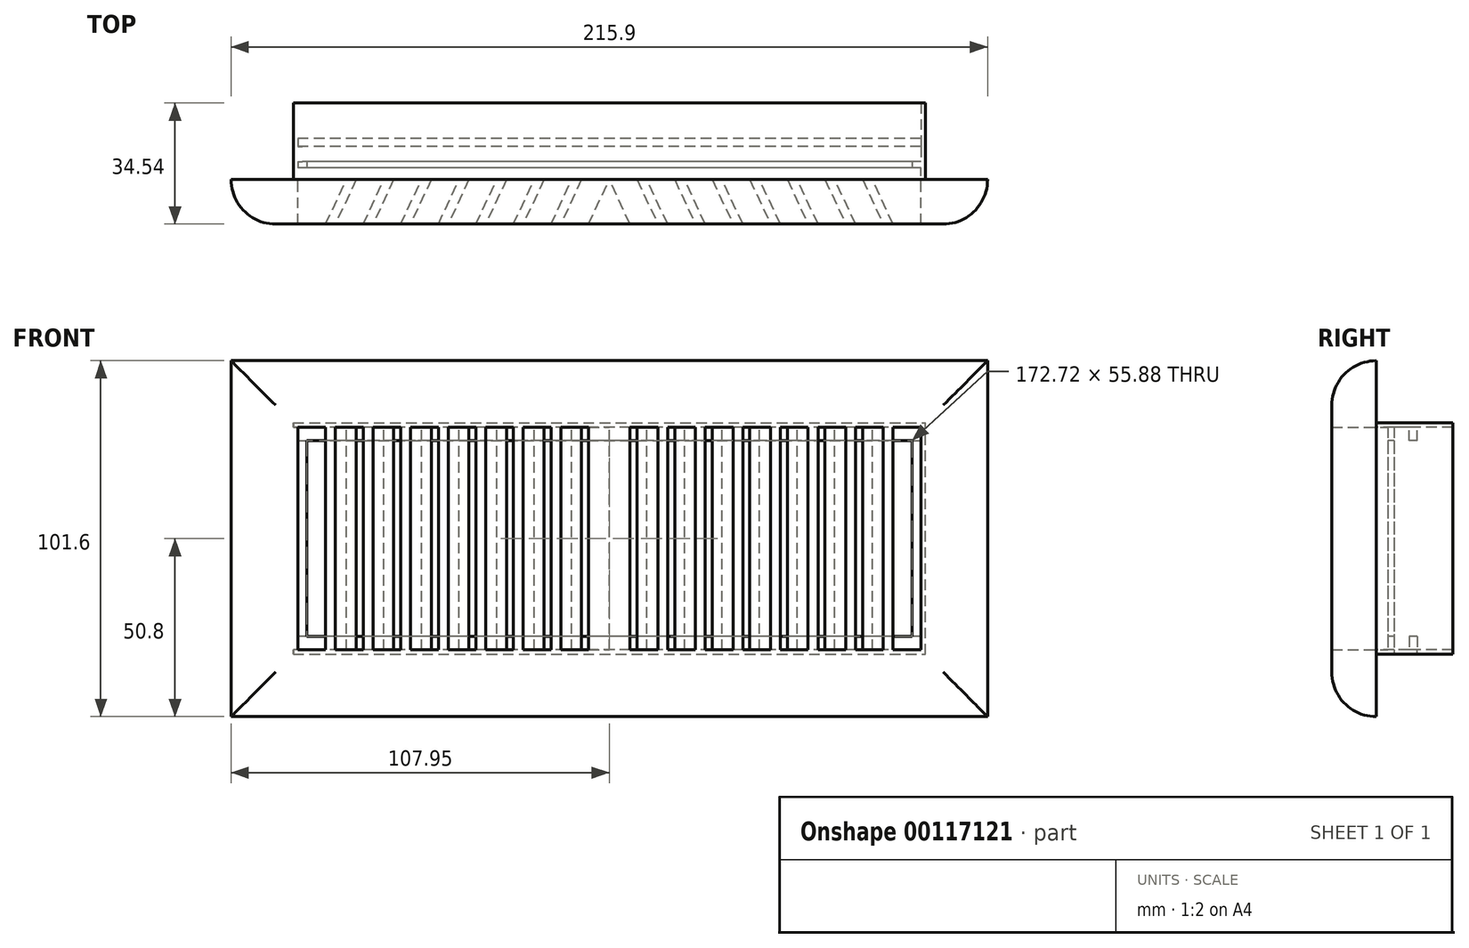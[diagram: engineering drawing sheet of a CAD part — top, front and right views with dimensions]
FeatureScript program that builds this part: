
annotation { "Feature Type Name" : "Feature", "Feature Type Description" : "" }
export const myFeature = defineFeature(function(context is Context, id is Id, definition is map)
    precondition{}
    {
        {
            var Q0;
            Q0=qCreatedBy(makeId("Front.planeOp"),FACE);
            var sketch = newSketch(context, id + "F0", { "sketchPlane" : qUnion([Q0])});
            skLineSegment(sketch, "E0.bottom", {"start": v(107.95, -50.8) * mm, "end": v(-107.95, -50.8) * mm});
            skLineSegment(sketch, "E0.top", {"start": v(107.95, 50.8) * mm, "end": v(-107.95, 50.8) * mm});
            skLineSegment(sketch, "E0.left", {"start": v(107.95, -50.8) * mm, "end": v(107.95, 50.8) * mm});
            skLineSegment(sketch, "E0.right", {"start": v(-107.95, -50.8) * mm, "end": v(-107.95, 50.8) * mm});
            skPoint(sketch, "E0.middle", {"position": v(0, 0) * mm});
            skLineSegment(sketch, "E1.bottom", {"start": v(88.9, -31.75) * mm, "end": v(-88.9, -31.75) * mm});
            skLineSegment(sketch, "E1.top", {"start": v(88.9, 31.75) * mm, "end": v(-88.9, 31.75) * mm});
            skLineSegment(sketch, "E1.left", {"start": v(88.9, -31.75) * mm, "end": v(88.9, 31.75) * mm});
            skLineSegment(sketch, "E1.right", {"start": v(-88.9, -31.75) * mm, "end": v(-88.9, 31.75) * mm});
            skSolve(sketch);
        }
        {
            var Q0;
            Q0=makeQuery(id+"F0.imprint","IMPRINT",FACE,{"disambiguationData":[TD([[makeQuery(id+"F0.imprint","IMPRINT",EDGE,{"derivedFrom":sQuery(id+"F0.wireOp",EDGE,"E0.bottom")}),-1.0]])]});
            extrude(context, id + "F1", {"entities" : qUnion([Q0]), "depth" : 12.7 * mm});
        }
        {
            var Q0;
            Q0=makeQuery(id+"F1.opExtrude","SWEPT_FACE",FACE,{"disambiguationData":[OSD([sQuery(id+"F0.wireOp",EDGE,"E0.top")])]});
            var sketch = newSketch(context, id + "F2", { "sketchPlane" : qUnion([Q0])});
            skLineSegment(sketch, "E2", {"start": v(-75.05, 0) * mm, "end": v(-80.97, -12.7) * mm});
            skLineSegment(sketch, "E3", {"start": v(-80.97, -12.7) * mm, "end": v(-78.17, -12.7) * mm});
            skLineSegment(sketch, "E4", {"start": v(-78.17, -12.7) * mm, "end": v(-72.25, 0) * mm});
            skLineSegment(sketch, "E5", {"start": v(-72.25, 0) * mm, "end": v(-75.05, 0) * mm});
            skLineSegment(sketch, "E6.1.0.0", {"start": v(-64.33, 0) * mm, "end": v(-70.25, -12.7) * mm});
            skLineSegment(sketch, "E6.1.0.1", {"start": v(-70.25, -12.7) * mm, "end": v(-67.45, -12.7) * mm});
            skLineSegment(sketch, "E6.1.0.2", {"start": v(-67.45, -12.7) * mm, "end": v(-61.53, 0) * mm});
            skLineSegment(sketch, "E6.1.0.3", {"start": v(-61.53, 0) * mm, "end": v(-64.33, 0) * mm});
            skLineSegment(sketch, "E6.2.0.0", {"start": v(-53.6, 0) * mm, "end": v(-59.53, -12.7) * mm});
            skLineSegment(sketch, "E6.2.0.1", {"start": v(-59.53, -12.7) * mm, "end": v(-56.73, -12.7) * mm});
            skLineSegment(sketch, "E6.2.0.2", {"start": v(-56.73, -12.7) * mm, "end": v(-50.8, 0) * mm});
            skLineSegment(sketch, "E6.2.0.3", {"start": v(-50.8, 0) * mm, "end": v(-53.6, 0) * mm});
            skLineSegment(sketch, "E6.3.0.0", {"start": v(-42.88, 0) * mm, "end": v(-48.8, -12.7) * mm});
            skLineSegment(sketch, "E6.3.0.1", {"start": v(-48.8, -12.7) * mm, "end": v(-46, -12.7) * mm});
            skLineSegment(sketch, "E6.3.0.2", {"start": v(-46, -12.7) * mm, "end": v(-40.08, 0) * mm});
            skLineSegment(sketch, "E6.3.0.3", {"start": v(-40.08, 0) * mm, "end": v(-42.88, 0) * mm});
            skLineSegment(sketch, "E6.4.0.0", {"start": v(-32.16, 0) * mm, "end": v(-38.08, -12.7) * mm});
            skLineSegment(sketch, "E6.4.0.1", {"start": v(-38.08, -12.7) * mm, "end": v(-35.28, -12.7) * mm});
            skLineSegment(sketch, "E6.4.0.2", {"start": v(-35.28, -12.7) * mm, "end": v(-29.36, 0) * mm});
            skLineSegment(sketch, "E6.4.0.3", {"start": v(-29.36, 0) * mm, "end": v(-32.16, 0) * mm});
            skLineSegment(sketch, "E6.5.0.0", {"start": v(-21.44, 0) * mm, "end": v(-27.36, -12.7) * mm});
            skLineSegment(sketch, "E6.5.0.1", {"start": v(-27.36, -12.7) * mm, "end": v(-24.56, -12.7) * mm});
            skLineSegment(sketch, "E6.5.0.2", {"start": v(-24.56, -12.7) * mm, "end": v(-18.64, 0) * mm});
            skLineSegment(sketch, "E6.5.0.3", {"start": v(-18.64, 0) * mm, "end": v(-21.44, 0) * mm});
            skLineSegment(sketch, "E6.6.0.0", {"start": v(-10.72, 0) * mm, "end": v(-16.64, -12.7) * mm});
            skLineSegment(sketch, "E6.6.0.1", {"start": v(-16.64, -12.7) * mm, "end": v(-13.84, -12.7) * mm});
            skLineSegment(sketch, "E6.6.0.2", {"start": v(-13.84, -12.7) * mm, "end": v(-7.92, 0) * mm});
            skLineSegment(sketch, "E6.6.0.3", {"start": v(-7.92, 0) * mm, "end": v(-10.72, 0) * mm});
            skLineSegment(sketch, "E6.direction1", {"start": v(-80.97, -12.7) * mm, "end": v(-70.25, -12.7) * mm, "construction": true});
            skLineSegment(sketch, "E7", {"start": v(75.05, 0) * mm, "end": v(80.97, -12.7) * mm});
            skLineSegment(sketch, "E8", {"start": v(80.97, -12.7) * mm, "end": v(78.17, -12.7) * mm});
            skLineSegment(sketch, "E9", {"start": v(78.17, -12.7) * mm, "end": v(72.25, 0) * mm});
            skLineSegment(sketch, "E10", {"start": v(72.25, 0) * mm, "end": v(75.05, 0) * mm});
            skLineSegment(sketch, "E11.1.0.0", {"start": v(70.25, -12.7) * mm, "end": v(67.45, -12.7) * mm});
            skLineSegment(sketch, "E11.1.0.1", {"start": v(64.33, 0) * mm, "end": v(70.25, -12.7) * mm});
            skLineSegment(sketch, "E11.1.0.2", {"start": v(61.53, 0) * mm, "end": v(64.33, 0) * mm});
            skLineSegment(sketch, "E11.1.0.3", {"start": v(67.45, -12.7) * mm, "end": v(61.53, 0) * mm});
            skLineSegment(sketch, "E11.2.0.0", {"start": v(59.53, -12.7) * mm, "end": v(56.73, -12.7) * mm});
            skLineSegment(sketch, "E11.2.0.1", {"start": v(53.6, 0) * mm, "end": v(59.53, -12.7) * mm});
            skLineSegment(sketch, "E11.2.0.2", {"start": v(50.8, 0) * mm, "end": v(53.6, 0) * mm});
            skLineSegment(sketch, "E11.2.0.3", {"start": v(56.73, -12.7) * mm, "end": v(50.8, 0) * mm});
            skLineSegment(sketch, "E11.3.0.0", {"start": v(48.8, -12.7) * mm, "end": v(46, -12.7) * mm});
            skLineSegment(sketch, "E11.3.0.1", {"start": v(42.88, 0) * mm, "end": v(48.8, -12.7) * mm});
            skLineSegment(sketch, "E11.3.0.2", {"start": v(40.08, 0) * mm, "end": v(42.88, 0) * mm});
            skLineSegment(sketch, "E11.3.0.3", {"start": v(46, -12.7) * mm, "end": v(40.08, 0) * mm});
            skLineSegment(sketch, "E11.4.0.0", {"start": v(38.08, -12.7) * mm, "end": v(35.28, -12.7) * mm});
            skLineSegment(sketch, "E11.4.0.1", {"start": v(32.16, 0) * mm, "end": v(38.08, -12.7) * mm});
            skLineSegment(sketch, "E11.4.0.2", {"start": v(29.36, 0) * mm, "end": v(32.16, 0) * mm});
            skLineSegment(sketch, "E11.4.0.3", {"start": v(35.28, -12.7) * mm, "end": v(29.36, 0) * mm});
            skLineSegment(sketch, "E11.5.0.0", {"start": v(27.36, -12.7) * mm, "end": v(24.56, -12.7) * mm});
            skLineSegment(sketch, "E11.5.0.1", {"start": v(21.44, 0) * mm, "end": v(27.36, -12.7) * mm});
            skLineSegment(sketch, "E11.5.0.2", {"start": v(18.64, 0) * mm, "end": v(21.44, 0) * mm});
            skLineSegment(sketch, "E11.5.0.3", {"start": v(24.56, -12.7) * mm, "end": v(18.64, 0) * mm});
            skLineSegment(sketch, "E11.6.0.0", {"start": v(16.64, -12.7) * mm, "end": v(13.84, -12.7) * mm});
            skLineSegment(sketch, "E11.6.0.1", {"start": v(10.72, 0) * mm, "end": v(16.64, -12.7) * mm});
            skLineSegment(sketch, "E11.6.0.2", {"start": v(7.92, 0) * mm, "end": v(10.72, 0) * mm});
            skLineSegment(sketch, "E11.6.0.3", {"start": v(13.84, -12.7) * mm, "end": v(7.92, 0) * mm});
            skLineSegment(sketch, "E11.direction1", {"start": v(78.17, -12.7) * mm, "end": v(67.45, -12.7) * mm, "construction": true});
            skLineSegment(sketch, "E12", {"start": v(0, 0) * mm, "end": v(0, -12.7) * mm, "construction": true});
            skLineSegment(sketch, "E13", {"start": v(0, 0) * mm, "end": v(-5.92, -12.7) * mm});
            skLineSegment(sketch, "E14", {"start": v(0, 0) * mm, "end": v(5.92, -12.7) * mm});
            skLineSegment(sketch, "E15", {"start": v(-5.92, -12.7) * mm, "end": v(5.92, -12.7) * mm});
            skSolve(sketch);
        }
        {
            var Q0;
            Q0 = qSketchRegion(id + "F2", true);
            extrude(context, id + "F3", {"entities" : qUnion([Q0]), "operationType" : NewBodyOperationType.ADD, "oppositeDirection" : true, "depth" : 101.6 * mm});
        }
        {
            var Q0;
            Q0=makeQuery(id+"F1.opExtrude","CAP_EDGE",EDGE,{"disambiguationData":[OSD([sQuery(id+"F0.wireOp",EDGE,"E0.top")])],"isStart":false});
            var Q1;
            Q1=makeQuery(id+"F1.opExtrude","CAP_EDGE",EDGE,{"disambiguationData":[OSD([sQuery(id+"F0.wireOp",EDGE,"E0.right")])],"isStart":false});
            var Q2;
            Q2=makeQuery(id+"F1.opExtrude","CAP_EDGE",EDGE,{"disambiguationData":[OSD([sQuery(id+"F0.wireOp",EDGE,"E0.bottom")])],"isStart":false});
            var Q3;
            Q3=makeQuery(id+"F1.opExtrude","CAP_EDGE",EDGE,{"disambiguationData":[OSD([sQuery(id+"F0.wireOp",EDGE,"E0.left")])],"isStart":false});
            fillet(context, id + "F4", {"entities" : qUnion([Q0, Q1, Q2, Q3]), "radius" : 12.7 * mm, "tangentPropagation" : true, "allowEdgeOverflow" : false});
        }
        {
            var Q0;
            Q0=makeQuery(id+"F3.boolean.opBoolean","MERGE",FACE,{"derivedFrom":[makeQuery(id+"F1.opExtrude","CAP_FACE",FACE,{"disambiguationData":[OSD([sQuery(id+"F0.wireOp",EDGE,"E0.bottom"),sQuery(id+"F0.wireOp",EDGE,"E0.top"),sQuery(id+"F0.wireOp",EDGE,"E0.left"),sQuery(id+"F0.wireOp",EDGE,"E0.right"),sQuery(id+"F0.wireOp",EDGE,"E1.bottom"),sQuery(id+"F0.wireOp",EDGE,"E1.top"),sQuery(id+"F0.wireOp",EDGE,"E1.left"),sQuery(id+"F0.wireOp",EDGE,"E1.right")])],"isStart":true}),makeQuery(id+"F3.opExtrude","SWEPT_FACE",FACE,{"disambiguationData":[OSD([sQuery(id+"F2.wireOp",EDGE,"E5")])]}),makeQuery(id+"F3.opExtrude","SWEPT_FACE",FACE,{"disambiguationData":[OSD([sQuery(id+"F2.wireOp",EDGE,"E6.1.0.3")])]}),makeQuery(id+"F3.opExtrude","SWEPT_FACE",FACE,{"disambiguationData":[OSD([sQuery(id+"F2.wireOp",EDGE,"E6.2.0.3")])]}),makeQuery(id+"F3.opExtrude","SWEPT_FACE",FACE,{"disambiguationData":[OSD([sQuery(id+"F2.wireOp",EDGE,"E6.3.0.3")])]}),makeQuery(id+"F3.opExtrude","SWEPT_FACE",FACE,{"disambiguationData":[OSD([sQuery(id+"F2.wireOp",EDGE,"E6.4.0.3")])]}),makeQuery(id+"F3.opExtrude","SWEPT_FACE",FACE,{"disambiguationData":[OSD([sQuery(id+"F2.wireOp",EDGE,"E6.5.0.3")])]}),makeQuery(id+"F3.opExtrude","SWEPT_FACE",FACE,{"disambiguationData":[OSD([sQuery(id+"F2.wireOp",EDGE,"E6.6.0.3")])]}),makeQuery(id+"F3.opExtrude","SWEPT_FACE",FACE,{"disambiguationData":[OSD([sQuery(id+"F2.wireOp",EDGE,"E10")])]}),makeQuery(id+"F3.opExtrude","SWEPT_FACE",FACE,{"disambiguationData":[OSD([sQuery(id+"F2.wireOp",EDGE,"E11.1.0.2")])]}),makeQuery(id+"F3.opExtrude","SWEPT_FACE",FACE,{"disambiguationData":[OSD([sQuery(id+"F2.wireOp",EDGE,"E11.2.0.2")])]}),makeQuery(id+"F3.opExtrude","SWEPT_FACE",FACE,{"disambiguationData":[OSD([sQuery(id+"F2.wireOp",EDGE,"E11.3.0.2")])]}),makeQuery(id+"F3.opExtrude","SWEPT_FACE",FACE,{"disambiguationData":[OSD([sQuery(id+"F2.wireOp",EDGE,"E11.4.0.2")])]}),makeQuery(id+"F3.opExtrude","SWEPT_FACE",FACE,{"disambiguationData":[OSD([sQuery(id+"F2.wireOp",EDGE,"E11.5.0.2")])]}),makeQuery(id+"F3.opExtrude","SWEPT_FACE",FACE,{"disambiguationData":[OSD([sQuery(id+"F2.wireOp",EDGE,"E11.6.0.2")])]})]});
            var sketch = newSketch(context, id + "F5", { "sketchPlane" : qUnion([Q0])});
            skLineSegment(sketch, "E16.bottom", {"start": v(90.17, -33.02) * mm, "end": v(-90.17, -33.02) * mm});
            skLineSegment(sketch, "E16.top", {"start": v(90.17, 33.02) * mm, "end": v(-90.17, 33.02) * mm});
            skLineSegment(sketch, "E16.right", {"start": v(-90.17, -33.02) * mm, "end": v(-90.17, 33.02) * mm});
            skPoint(sketch, "E16.middle", {"position": v(0, 0) * mm});
            skLineSegment(sketch, "E17.bottom", {"start": v(88.9, -31.75) * mm, "end": v(-88.9, -31.75) * mm});
            skLineSegment(sketch, "E17.top", {"start": v(88.9, 31.75) * mm, "end": v(-88.9, 31.75) * mm});
            skLineSegment(sketch, "E17.right", {"start": v(-88.9, -31.75) * mm, "end": v(-88.9, 31.75) * mm});
            skLineSegment(sketch, "E18", {"start": v(88.9, 31.75) * mm, "end": v(90.17, 31.75) * mm});
            skLineSegment(sketch, "E19", {"start": v(90.17, 31.75) * mm, "end": v(90.17, 33.02) * mm});
            skLineSegment(sketch, "E20", {"start": v(88.9, -31.75) * mm, "end": v(90.17, -31.75) * mm});
            skLineSegment(sketch, "E21", {"start": v(90.17, -31.75) * mm, "end": v(90.17, -33.02) * mm});
            skSolve(sketch);
        }
        {
            var Q0;
            Q0 = qSketchRegion(id + "F5", true);
            extrude(context, id + "F6", {"entities" : qUnion([Q0]), "operationType" : NewBodyOperationType.ADD, "depth" : 3.3 * mm});
        }
        {
            var Q0;
            Q0=makeQuery(id+"F6.opExtrude","CAP_FACE",FACE,{"disambiguationData":[OSD([sQuery(id+"F5.wireOp",EDGE,"E16.bottom"),sQuery(id+"F5.wireOp",EDGE,"E16.top"),sQuery(id+"F5.wireOp",EDGE,"E16.right"),sQuery(id+"F5.wireOp",EDGE,"E17.bottom"),sQuery(id+"F5.wireOp",EDGE,"E17.top"),sQuery(id+"F5.wireOp",EDGE,"E17.right"),sQuery(id+"F5.wireOp",EDGE,"E18"),sQuery(id+"F5.wireOp",EDGE,"E19"),sQuery(id+"F5.wireOp",EDGE,"E20"),sQuery(id+"F5.wireOp",EDGE,"E21")])],"isStart":false});
            var sketch = newSketch(context, id + "F7", { "sketchPlane" : qUnion([Q0])});
            skLineSegment(sketch, "E22.bottom", {"start": v(-90.17, 33.02) * mm, "end": v(88.9, 33.02) * mm});
            skLineSegment(sketch, "E22.top", {"start": v(-90.17, -33.02) * mm, "end": v(88.9, -33.02) * mm});
            skLineSegment(sketch, "E22.left", {"start": v(-90.17, 33.02) * mm, "end": v(-90.17, -33.02) * mm});
            skLineSegment(sketch, "E22.right", {"start": v(88.9, 33.02) * mm, "end": v(88.9, -33.02) * mm});
            skLineSegment(sketch, "E23.bottom", {"start": v(-86.36, 27.94) * mm, "end": v(86.36, 27.94) * mm});
            skLineSegment(sketch, "E23.top", {"start": v(-86.36, -27.94) * mm, "end": v(86.36, -27.94) * mm});
            skLineSegment(sketch, "E23.left", {"start": v(-86.36, 27.94) * mm, "end": v(-86.36, -27.94) * mm});
            skLineSegment(sketch, "E23.right", {"start": v(86.36, 27.94) * mm, "end": v(86.36, -27.94) * mm});
            skSolve(sketch);
        }
        {
            var Q0;
            Q0 = qSketchRegion(id + "F7", true);
            extrude(context, id + "F8", {"entities" : qUnion([Q0]), "operationType" : NewBodyOperationType.ADD, "depth" : 1.78 * mm});
        }
        {
            var Q0;
            Q0=makeQuery(id+"F8.opExtrude","CAP_FACE",FACE,{"disambiguationData":[OSD([sQuery(id+"F7.wireOp",EDGE,"E22.bottom"),sQuery(id+"F7.wireOp",EDGE,"E22.top"),sQuery(id+"F7.wireOp",EDGE,"E22.left"),sQuery(id+"F7.wireOp",EDGE,"E22.right"),sQuery(id+"F7.wireOp",EDGE,"E23.bottom"),sQuery(id+"F7.wireOp",EDGE,"E23.top"),sQuery(id+"F7.wireOp",EDGE,"E23.left"),sQuery(id+"F7.wireOp",EDGE,"E23.right")])],"isStart":false});
            var sketch = newSketch(context, id + "F9", { "sketchPlane" : qUnion([Q0])});
            skLineSegment(sketch, "E24.bottom", {"start": v(-90.17, 33.02) * mm, "end": v(88.9, 33.02) * mm});
            skLineSegment(sketch, "E24.top", {"start": v(-90.17, -33.02) * mm, "end": v(88.9, -33.02) * mm});
            skLineSegment(sketch, "E24.left", {"start": v(-90.17, 33.02) * mm, "end": v(-90.17, -33.02) * mm});
            skLineSegment(sketch, "E25.bottom", {"start": v(-88.9, 31.75) * mm, "end": v(87.63, 31.75) * mm});
            skLineSegment(sketch, "E25.top", {"start": v(-88.9, -31.75) * mm, "end": v(87.63, -31.75) * mm});
            skLineSegment(sketch, "E25.left", {"start": v(-88.9, 31.75) * mm, "end": v(-88.9, -31.75) * mm});
            skLineSegment(sketch, "E26", {"start": v(88.9, -33.02) * mm, "end": v(90.18, -33.02) * mm});
            skLineSegment(sketch, "E27", {"start": v(90.18, -33.02) * mm, "end": v(90.18, -31.75) * mm});
            skLineSegment(sketch, "E28", {"start": v(90.18, -31.75) * mm, "end": v(87.63, -31.75) * mm});
            skLineSegment(sketch, "E29", {"start": v(88.9, 33.02) * mm, "end": v(90.17, 33.02) * mm});
            skLineSegment(sketch, "E30", {"start": v(90.17, 33.02) * mm, "end": v(90.17, 31.75) * mm});
            skLineSegment(sketch, "E31", {"start": v(90.17, 31.75) * mm, "end": v(87.63, 31.75) * mm});
            skSolve(sketch);
        }
        {
            var Q0;
            {var subQ5=sQuery(id+"F9.wireOp",EDGE,"E24.bottom");Q0=makeQuery(id+"F9.imprint","IMPRINT",FACE,{"disambiguationData":[TD([[makeQuery(id+"F9.imprint","IMPRINT",EDGE,{"derivedFrom":subQ5}),1.0]])]});}
            var Q1;
            {var subQ0=sQuery(id+"F9.wireOp",EDGE,"E29");Q1=makeQuery(id+"F9.imprint","IMPRINT",FACE,{"disambiguationData":[TD([[makeQuery(id+"F9.imprint","IMPRINT",EDGE,{"derivedFrom":subQ0}),-1.0]])]});}
            var Q2;
            {var subQ0=sQuery(id+"F9.wireOp",EDGE,"E26");Q2=makeQuery(id+"F9.imprint","IMPRINT",FACE,{"disambiguationData":[TD([[makeQuery(id+"F9.imprint","IMPRINT",EDGE,{"derivedFrom":subQ0}),1.0]])]});}
            extrude(context, id + "F10", {"entities" : qUnion([Q0, Q1, Q2]), "operationType" : NewBodyOperationType.ADD, "depth" : 4.32 * mm});
        }
        {
            var Q0;
            {var subQ0=sQuery(id+"F5.wireOp",EDGE,"E21");var subQ1=sQuery(id+"F5.wireOp",EDGE,"E20");var subQ2=sQuery(id+"F5.wireOp",EDGE,"E17.bottom");var subQ3=sQuery(id+"F5.wireOp",EDGE,"E16.bottom");Q0=makeQuery(id+"F8.boolean.opBoolean","SPLIT",FACE,{"disambiguationData":[TD([makeQuery(id+"F1.opExtrude","SWEPT_FACE",FACE,{"disambiguationData":[OSD([sQuery(id+"F0.wireOp",EDGE,"E1.bottom")])]})])],"derivedFrom":makeQuery(id+"F6.opExtrude","CAP_FACE",FACE,{"disambiguationData":[OSD([subQ3,sQuery(id+"F5.wireOp",EDGE,"E16.top"),sQuery(id+"F5.wireOp",EDGE,"E16.right"),subQ2,sQuery(id+"F5.wireOp",EDGE,"E17.top"),sQuery(id+"F5.wireOp",EDGE,"E17.right"),sQuery(id+"F5.wireOp",EDGE,"E18"),sQuery(id+"F5.wireOp",EDGE,"E19"),subQ1,subQ0])],"isStart":false})});}
            var sketch = newSketch(context, id + "F11", { "sketchPlane" : qUnion([Q0])});
            skLineSegment(sketch, "E32.bottom", {"start": v(88.9, -33.02) * mm, "end": v(90.17, -33.02) * mm});
            skLineSegment(sketch, "E32.top", {"start": v(88.9, -31.75) * mm, "end": v(90.17, -31.75) * mm});
            skLineSegment(sketch, "E32.left", {"start": v(88.9, -33.02) * mm, "end": v(88.9, -31.75) * mm});
            skLineSegment(sketch, "E32.right", {"start": v(90.17, -33.02) * mm, "end": v(90.17, -31.75) * mm});
            skSolve(sketch);
        }
        {
            var Q0;
            Q0 = qSketchRegion(id + "F11", true);
            extrude(context, id + "F12", {"entities" : qUnion([Q0]), "operationType" : NewBodyOperationType.ADD, "depth" : 1.78 * mm});
        }
        {
            var Q0;
            Q0=makeQuery(id+"F10.opExtrude","CAP_FACE",FACE,{"disambiguationData":[OSD([sQuery(id+"F9.wireOp",EDGE,"E24.bottom"),sQuery(id+"F9.wireOp",EDGE,"E24.top"),sQuery(id+"F9.wireOp",EDGE,"E24.left"),sQuery(id+"F9.wireOp",EDGE,"E25.bottom"),sQuery(id+"F9.wireOp",EDGE,"E25.top"),sQuery(id+"F9.wireOp",EDGE,"E25.left"),sQuery(id+"F9.wireOp",EDGE,"E26"),sQuery(id+"F9.wireOp",EDGE,"E27"),sQuery(id+"F9.wireOp",EDGE,"E28"),sQuery(id+"F9.wireOp",EDGE,"E29"),sQuery(id+"F9.wireOp",EDGE,"E30"),sQuery(id+"F9.wireOp",EDGE,"E31")])],"isStart":false});
            var sketch = newSketch(context, id + "F13", { "sketchPlane" : qUnion([Q0])});
            skLineSegment(sketch, "E33.bottom", {"start": v(-90.17, 33.02) * mm, "end": v(88.9, 33.02) * mm});
            skLineSegment(sketch, "E33.top", {"start": v(-90.17, -33.02) * mm, "end": v(88.9, -33.02) * mm});
            skLineSegment(sketch, "E34.bottom", {"start": v(-84.84, 27.94) * mm, "end": v(88.9, 27.94) * mm});
            skLineSegment(sketch, "E34.top", {"start": v(-84.84, -27.94) * mm, "end": v(88.9, -27.94) * mm});
            skLineSegment(sketch, "E35", {"start": v(-84.84, 27.94) * mm, "end": v(-90.17, 27.94) * mm});
            skLineSegment(sketch, "E36", {"start": v(-90.17, 27.94) * mm, "end": v(-90.17, 33.02) * mm});
            skLineSegment(sketch, "E37", {"start": v(-84.84, -27.94) * mm, "end": v(-90.17, -27.94) * mm});
            skLineSegment(sketch, "E38", {"start": v(-90.17, -27.94) * mm, "end": v(-90.17, -33.02) * mm});
            skLineSegment(sketch, "E39.bottom", {"start": v(-90.17, 27.94) * mm, "end": v(-88.9, 27.94) * mm});
            skLineSegment(sketch, "E39.top", {"start": v(-90.17, -27.94) * mm, "end": v(-88.9, -27.94) * mm});
            skLineSegment(sketch, "E39.left", {"start": v(-90.17, 27.94) * mm, "end": v(-90.17, -27.94) * mm});
            skLineSegment(sketch, "E39.right", {"start": v(-88.9, 27.94) * mm, "end": v(-88.9, -27.94) * mm});
            skLineSegment(sketch, "E40", {"start": v(88.9, -27.94) * mm, "end": v(88.9, -33.02) * mm});
            skLineSegment(sketch, "E41", {"start": v(88.9, 27.94) * mm, "end": v(88.9, 33.02) * mm});
            skSolve(sketch);
        }
        {
            var Q0;
            Q0 = qSketchRegion(id + "F13", true);
            extrude(context, id + "F14", {"entities" : qUnion([Q0]), "operationType" : NewBodyOperationType.ADD, "depth" : 2.3 * mm});
        }
        {
            var Q0;
            Q0=makeQuery(id+"F14.opExtrude","SWEPT_FACE",FACE,{"disambiguationData":[OSD([sQuery(id+"F13.wireOp",EDGE,"E34.top"),sQuery(id+"F13.wireOp",EDGE,"E37"),sQuery(id+"F13.wireOp",EDGE,"TGxW7JvE-hO0u-tt39-ioUT-bYuH0o1wrKsi")])]});
            var sketch = newSketch(context, id + "F15", { "sketchPlane" : qUnion([Q0])});
            skSolve(sketch);
        }
        {
            var Q0;
            Q0=makeQuery(id+"Fv8F5Soem3vfvmW_1.boolean.opBoolean","MERGE",FACE,{"derivedFrom":[makeQuery(id+"F14.opExtrude","CAP_FACE",FACE,{"disambiguationData":[OSD([sQuery(id+"F13.wireOp",EDGE,"E33.bottom"),sQuery(id+"F13.wireOp",EDGE,"E33.top"),sQuery(id+"F13.wireOp",EDGE,"E34.bottom"),sQuery(id+"F13.wireOp",EDGE,"E34.top"),sQuery(id+"F13.wireOp",EDGE,"E35"),sQuery(id+"F13.wireOp",EDGE,"E36"),sQuery(id+"F13.wireOp",EDGE,"E37"),sQuery(id+"F13.wireOp",EDGE,"E38"),sQuery(id+"F13.wireOp",EDGE,"E39.left"),sQuery(id+"F13.wireOp",EDGE,"E39.right"),sQuery(id+"F13.wireOp",EDGE,"TGxW7JvE-hO0u-tt39-ioUT-bYuH0o1wrKsi"),sQuery(id+"F13.wireOp",EDGE,"xJwFBrmR-DKHQ-Ms6E-cGLF-1sDl0en4KIHk"),sQuery(id+"F13.wireOp",EDGE,"KjPjYPhn-M9NA-BWyU-6eae-7lh8KEkwCyoe"),sQuery(id+"F13.wireOp",EDGE,"DDPbrne3-7nOW-QVff-d2O1-u6GeuogKL0BI")])],"isStart":false}),makeQuery(id+"Fv8F5Soem3vfvmW_1.opExtrude","SWEPT_FACE",FACE,{"disambiguationData":[OSD([sQuery(id+"F15.wireOp",EDGE,"I5fvG48v-rP8C-mtnB-2jEv-sWBCkAZKz6mY.bottom")])]})]});
            var sketch = newSketch(context, id + "F16", { "sketchPlane" : qUnion([Q0])});
            skLineSegment(sketch, "E42.bottom", {"start": v(-90.17, 33.02) * mm, "end": v(90.17, 33.02) * mm});
            skLineSegment(sketch, "E42.top", {"start": v(-90.17, -33.02) * mm, "end": v(90.17, -33.02) * mm});
            skLineSegment(sketch, "E42.left", {"start": v(-90.17, 33.02) * mm, "end": v(-90.17, -33.02) * mm});
            skLineSegment(sketch, "E43.bottom", {"start": v(-88.9, 31.75) * mm, "end": v(84.62, 31.75) * mm});
            skLineSegment(sketch, "E43.top", {"start": v(-88.9, -31.75) * mm, "end": v(84.62, -31.75) * mm});
            skLineSegment(sketch, "E43.left", {"start": v(-88.9, 31.75) * mm, "end": v(-88.9, -31.75) * mm});
            skLineSegment(sketch, "E44", {"start": v(84.62, 31.75) * mm, "end": v(90.17, 31.75) * mm});
            skLineSegment(sketch, "E45", {"start": v(90.17, 33.02) * mm, "end": v(90.17, 31.75) * mm});
            skLineSegment(sketch, "E46", {"start": v(84.62, -31.75) * mm, "end": v(90.17, -31.75) * mm});
            skLineSegment(sketch, "E47", {"start": v(90.17, -33.02) * mm, "end": v(90.17, -31.75) * mm});
            skSolve(sketch);
        }
        {
            var Q0;
            Q0 = qSketchRegion(id + "F16", true);
            extrude(context, id + "F17", {"entities" : qUnion([Q0]), "operationType" : NewBodyOperationType.ADD, "depth" : 10.16 * mm});
        }
        {
            var Q0;
            {var subQ0=sQuery(id+"F5.wireOp",EDGE,"E18");var subQ1=sQuery(id+"F5.wireOp",EDGE,"E17.top");var subQ2=sQuery(id+"F5.wireOp",EDGE,"E19");var subQ3=sQuery(id+"F5.wireOp",EDGE,"E16.top");Q0=makeQuery(id+"F8.boolean.opBoolean","SPLIT",FACE,{"disambiguationData":[TD([makeQuery(id+"F1.opExtrude","SWEPT_FACE",FACE,{"disambiguationData":[OSD([sQuery(id+"F0.wireOp",EDGE,"E1.top")])]})])],"derivedFrom":makeQuery(id+"F6.opExtrude","CAP_FACE",FACE,{"disambiguationData":[OSD([sQuery(id+"F5.wireOp",EDGE,"E16.bottom"),subQ3,sQuery(id+"F5.wireOp",EDGE,"E16.right"),sQuery(id+"F5.wireOp",EDGE,"E17.bottom"),subQ1,sQuery(id+"F5.wireOp",EDGE,"E17.right"),subQ0,subQ2,sQuery(id+"F5.wireOp",EDGE,"E20"),sQuery(id+"F5.wireOp",EDGE,"E21")])],"isStart":false})});}
            var sketch = newSketch(context, id + "F18", { "sketchPlane" : qUnion([Q0])});
            skLineSegment(sketch, "E48.bottom", {"start": v(88.9, 33.02) * mm, "end": v(90.17, 33.02) * mm});
            skLineSegment(sketch, "E48.top", {"start": v(88.9, 31.75) * mm, "end": v(90.17, 31.75) * mm});
            skLineSegment(sketch, "E48.left", {"start": v(88.9, 33.02) * mm, "end": v(88.9, 31.75) * mm});
            skLineSegment(sketch, "E48.right", {"start": v(90.17, 33.02) * mm, "end": v(90.17, 31.75) * mm});
            skSolve(sketch);
        }
        {
            var Q0;
            Q0 = qSketchRegion(id + "F18", true);
            extrude(context, id + "F19", {"entities" : qUnion([Q0]), "operationType" : NewBodyOperationType.ADD, "depth" : 1.78 * mm});
        }
        {
            var Q0;
            {var subQ0=sQuery(id+"F9.wireOp",EDGE,"E27");var subQ1=sQuery(id+"F9.wireOp",EDGE,"E26");var subQ2=sQuery(id+"F9.wireOp",EDGE,"E24.top");var subQ4=sQuery(id+"F9.wireOp",EDGE,"E28");Q0=makeQuery(id+"F14.boolean.opBoolean","SPLIT",FACE,{"disambiguationData":[TD([makeQuery(id+"F6.opExtrude","SWEPT_FACE",FACE,{"disambiguationData":[OSD([sQuery(id+"F5.wireOp",EDGE,"E16.bottom")])]})])],"derivedFrom":makeQuery(id+"F10.opExtrude","CAP_FACE",FACE,{"disambiguationData":[OSD([sQuery(id+"F9.wireOp",EDGE,"E24.bottom"),subQ2,sQuery(id+"F9.wireOp",EDGE,"E24.left"),sQuery(id+"F9.wireOp",EDGE,"E25.bottom"),sQuery(id+"F9.wireOp",EDGE,"E25.top"),sQuery(id+"F9.wireOp",EDGE,"E25.left"),subQ1,subQ0,subQ4,sQuery(id+"F9.wireOp",EDGE,"E29"),sQuery(id+"F9.wireOp",EDGE,"E30"),sQuery(id+"F9.wireOp",EDGE,"E31")])],"isStart":false})});}
            var sketch = newSketch(context, id + "F20", { "sketchPlane" : qUnion([Q0])});
            skLineSegment(sketch, "E49.bottom", {"start": v(88.9, -33.02) * mm, "end": v(90.18, -33.02) * mm});
            skLineSegment(sketch, "E49.top", {"start": v(88.9, -31.75) * mm, "end": v(90.18, -31.75) * mm});
            skLineSegment(sketch, "E49.left", {"start": v(88.9, -33.02) * mm, "end": v(88.9, -31.75) * mm});
            skLineSegment(sketch, "E49.right", {"start": v(90.18, -33.02) * mm, "end": v(90.18, -31.75) * mm});
            skSolve(sketch);
        }
        {
            var Q0;
            {var subQ2=sQuery(id+"F9.wireOp",EDGE,"E30");var subQ3=sQuery(id+"F9.wireOp",EDGE,"E29");var subQ4=sQuery(id+"F9.wireOp",EDGE,"E24.bottom");var subQ5=sQuery(id+"F9.wireOp",EDGE,"E31");Q0=makeQuery(id+"F14.boolean.opBoolean","SPLIT",FACE,{"disambiguationData":[TD([makeQuery(id+"F6.opExtrude","SWEPT_FACE",FACE,{"disambiguationData":[OSD([sQuery(id+"F5.wireOp",EDGE,"E16.top")])]})])],"derivedFrom":makeQuery(id+"F10.opExtrude","CAP_FACE",FACE,{"disambiguationData":[OSD([subQ4,sQuery(id+"F9.wireOp",EDGE,"E24.top"),sQuery(id+"F9.wireOp",EDGE,"E24.left"),sQuery(id+"F9.wireOp",EDGE,"E25.bottom"),sQuery(id+"F9.wireOp",EDGE,"E25.top"),sQuery(id+"F9.wireOp",EDGE,"E25.left"),sQuery(id+"F9.wireOp",EDGE,"E26"),sQuery(id+"F9.wireOp",EDGE,"E27"),sQuery(id+"F9.wireOp",EDGE,"E28"),subQ3,subQ2,subQ5])],"isStart":false})});}
            var sketch = newSketch(context, id + "F21", { "sketchPlane" : qUnion([Q0])});
            skLineSegment(sketch, "E50.bottom", {"start": v(88.9, 31.75) * mm, "end": v(90.17, 31.75) * mm});
            skLineSegment(sketch, "E50.top", {"start": v(88.9, 33.02) * mm, "end": v(90.17, 33.02) * mm});
            skLineSegment(sketch, "E50.left", {"start": v(88.9, 31.75) * mm, "end": v(88.9, 33.02) * mm});
            skLineSegment(sketch, "E50.right", {"start": v(90.17, 31.75) * mm, "end": v(90.17, 33.02) * mm});
            skSolve(sketch);
        }
        {
            var Q0;
            Q0 = qSketchRegion(id + "F21", true);
            var Q1;
            Q1 = qSketchRegion(id + "F20", true);
            extrude(context, id + "F22", {"entities" : qUnion([Q0, Q1]), "operationType" : NewBodyOperationType.ADD, "depth" : 2.3 * mm});
        }
    });
